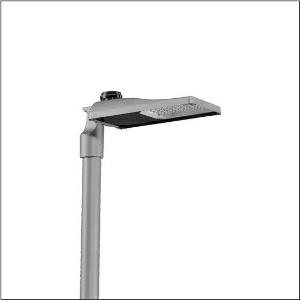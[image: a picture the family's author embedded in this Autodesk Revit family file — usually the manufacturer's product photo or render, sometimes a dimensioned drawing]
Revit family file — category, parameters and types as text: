
# Revit family: streetlight_sl_31_mini___st1_0a_5xh2d35n08ja_775f
name_source: partatom
category: Lighting Fixtures
units: mm (PartAtom-declared; Revit-internal decimal feet)

## family parameters
Cut with Voids When Loaded = No
Host = Face
Light Source = No
Part Type = Normal
Room Calculation Point = No
Round Connector Dimension = Use Diameter
Shared = No

## types (1)
- --- (1 x LED, 12140 lm, 81.1 W, 3000K)
    Apparent Load = 81 VA
    CIE Flux Codes = 40 73 97 100 100
    Color Rendering = 70
    Color Temperature = 3000K
    Default Elevation = 1800 mm
    Description = Streetlight SL 31 mini NEMA (7pin), Desk-Remote mast luminaire for post-top, side-entry; light control with lens of PMMA; light distribution: ST1.0a, direct asymmetric distribution, for standard-compliant lighting for roads and squares; LED: luminous flux: 12.140lm, light colour: 730, colour temperature: 3000K; luminous efficacy: 149,7lm/W; control: pre-setting: linear dimming characteristic, flexible luminous flux parameterisation, time-dependent luminous flux control, constant luminous flux control, intelligent temperature release in ECG and LED module, overheat protection; luminaire housing, of diecast aluminium, Siteco® metallic grey (DB 702S), corrosivity category C5 high according to DIN EN ISO 12944; cover of toughened safety glass, transparent, mast flange of diecast aluminium, Siteco® metallic grey (DB 702S), spigot size: 76/60mm, mast flange included unmounted; with cable H07RN-F 3x 1.5mm², cable length: 10,5m, connection cable pre-assembled; mains connection: 220..240V, AC, 50/60Hz; power consumption (at start of service life): 81,1W / (at end of service life): 88,3W / (with reduced operation 50%): 36,4W; protection rating (complete): IP66; insulation class (complete): insulation class I (protective earthing); impact resistance: IK10; certification: CE, ENEC, ENEC+, VDE, UKCA; permissible operating ambient temperature for outdoor applications: -40..+50°C; packaging unit: 1 piece

Light Distribution: ST1.0a
    Height = 76 mm
    Lamp = 1 x LED
    Lamp Light Flux = 12140 lm
    Lamp Power = 81.1 W
    Lamp count = 1
    Length = 547 mm
    Luminous efficacy = 150 lm/W
    Manufacturer = Siteco
    ModVariant = No
    Model = 5XH2D35N08JA
    Number of Poles = 1
    OnlyDefault = Yes
    Power Factor = 1
    Product Name = Streetlight SL 31 mini | ST1.0a
    Product group = mast luminaire | pylon top
    ProductGroupID = 6100
    Protection Class = Protection class I
    Protection Degree = IP 66
    RLX_Detail_Level = 1
    RLX_Emergency_Light_Flux = 0 lm
    RLX_Emergency_Type = 0
    RLX_Emergency_Type_DB = No
    RlxData = <blob elided: 40289 chars, md5=174ae342>
    Socket = socket
    Standby Power = 0 W
    System Light Flux = 12140 lm
    System Power = 81 W
    Type Comments = factory setting: luminous flux: 100 % | dim-lin: 254 | 860 mA
    Type Image = l_1300322.jpg
    URL = http://relux.com
    VarID = @adj_050686
    Voltage = 0 V
    Weight = 0.00 kg
    Width = 265 mm

## geometry (parser evidence)
native form markers: Blend x4, Sweep x9
no freeform markers — native parametric forms only
